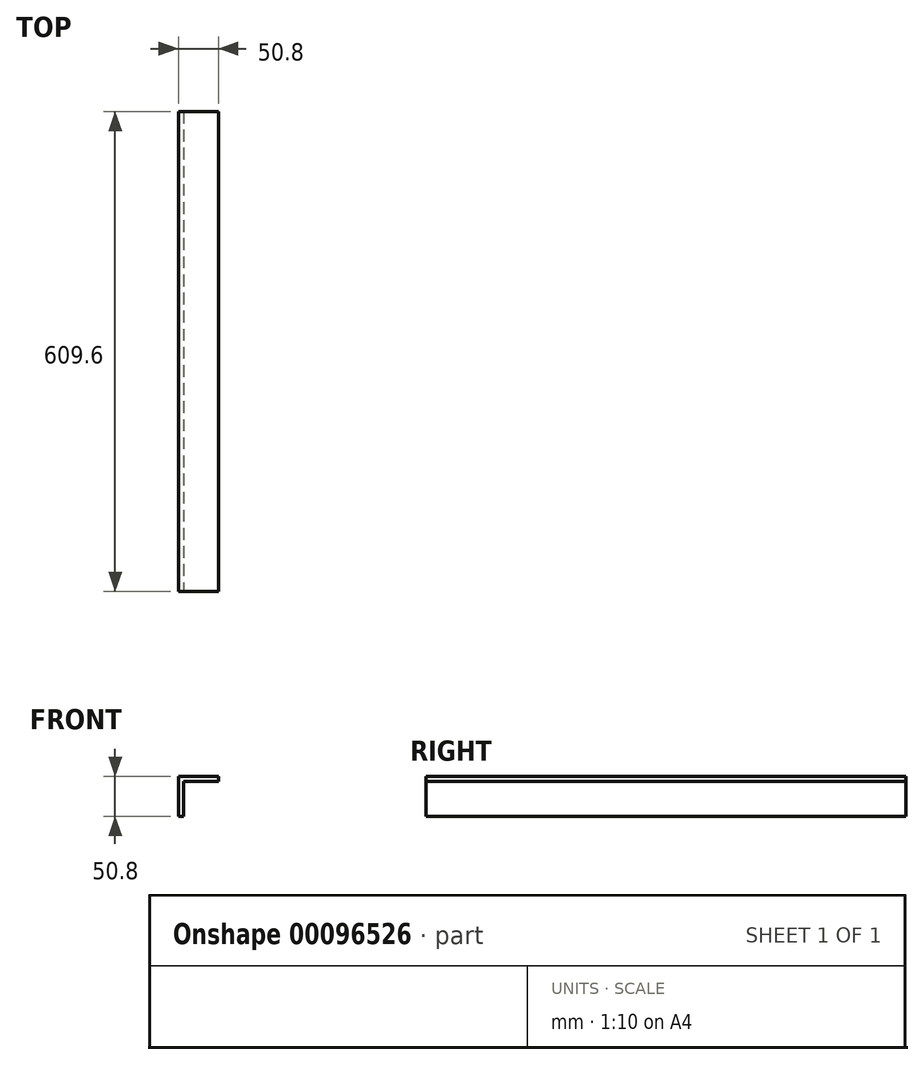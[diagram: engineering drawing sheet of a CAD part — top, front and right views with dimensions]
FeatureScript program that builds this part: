
annotation { "Feature Type Name" : "Feature", "Feature Type Description" : "" }
export const myFeature = defineFeature(function(context is Context, id is Id, definition is map)
    precondition{}
    {
        {
            var Q0;
            Q0=qCreatedBy(makeId("Front.planeOp"),FACE);
            var sketch = newSketch(context, id + "F0", { "sketchPlane" : qUnion([Q0])});
            skLineSegment(sketch, "E0", {"start": v(0, 0) * mm, "end": v(-50.8, 0) * mm});
            skLineSegment(sketch, "E1", {"start": v(-50.8, 0) * mm, "end": v(-50.8, -50.8) * mm});
            skLineSegment(sketch, "E2.0", {"start": v(-44.45, -6.35) * mm, "end": v(-44.45, -50.8) * mm});
            skLineSegment(sketch, "E2.1", {"start": v(0, -6.35) * mm, "end": v(-44.45, -6.35) * mm});
            skLineSegment(sketch, "E3", {"start": v(0, -6.35) * mm, "end": v(0, 0) * mm});
            skLineSegment(sketch, "E4", {"start": v(-50.8, -50.8) * mm, "end": v(-44.45, -50.8) * mm});
            skSolve(sketch);
        }
        {
            var Q0;
            Q0=qSketchRegion(id+"F0",true);
            extrude(context, id + "F1", {"entities" : qUnion([Q0]), "oppositeDirection" : true, "depth" : 609.6 * mm});
        }
    });
